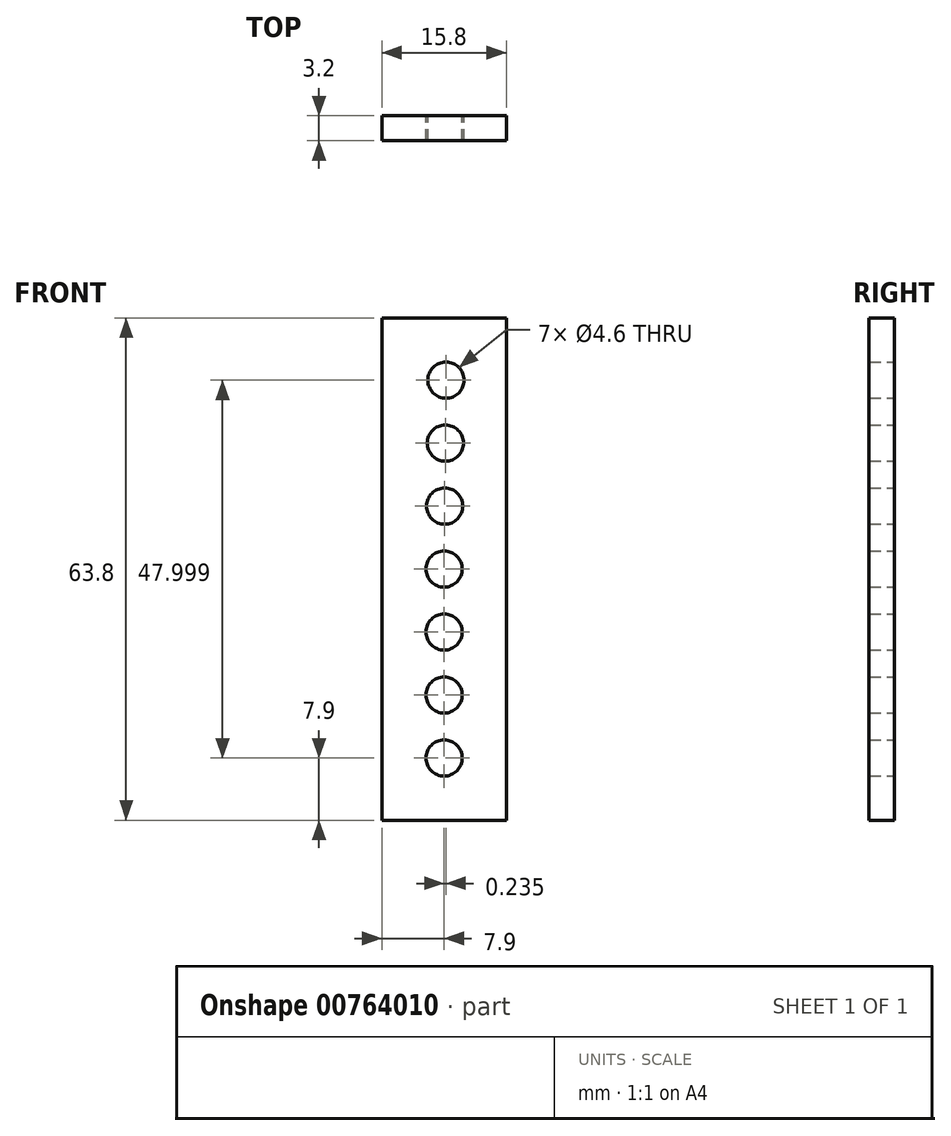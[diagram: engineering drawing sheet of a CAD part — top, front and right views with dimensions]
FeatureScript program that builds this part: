
annotation { "Feature Type Name" : "Feature", "Feature Type Description" : "" }
export const myFeature = defineFeature(function(context is Context, id is Id, definition is map)
    precondition{}
    {
        {
            var Q0;
            Q0=qCreatedBy(makeId("Front.planeOp"),FACE);
            var sketch = newSketch(context, id + "F0", { "sketchPlane" : qUnion([Q0])});
            skLineSegment(sketch, "E0.bottom", {"start": v(7.9, 31.9) * mm, "end": v(-7.9, 31.9) * mm});
            skLineSegment(sketch, "E0.top", {"start": v(7.9, -31.9) * mm, "end": v(-7.9, -31.9) * mm});
            skLineSegment(sketch, "E0.left", {"start": v(7.9, 31.9) * mm, "end": v(7.9, -31.9) * mm});
            skLineSegment(sketch, "E0.right", {"start": v(-7.9, 31.9) * mm, "end": v(-7.9, -31.9) * mm});
            skPoint(sketch, "E0.middle", {"position": v(0, 0) * mm});
            skCircle(sketch, "E1", {"center": v(0, 0) * mm, "radius": 2.3 * mm});
            skCircle(sketch, "E2.1.0.0", {"center": v(0, -8) * mm, "radius": 2.3 * mm});
            skCircle(sketch, "E2.2.0.0", {"center": v(0, -16) * mm, "radius": 2.3 * mm});
            skCircle(sketch, "E2.3.0.0", {"center": v(0, -24) * mm, "radius": 2.3 * mm});
            skLineSegment(sketch, "E2.direction1", {"start": v(0, 0) * mm, "end": v(0, -8) * mm, "construction": true});
            skCircle(sketch, "E3.1.0.0", {"center": v(0.08, 8) * mm, "radius": 2.3 * mm});
            skCircle(sketch, "E3.2.0.0", {"center": v(0.16, 16) * mm, "radius": 2.3 * mm});
            skCircle(sketch, "E3.3.0.0", {"center": v(0.24, 24) * mm, "radius": 2.3 * mm});
            skLineSegment(sketch, "E3.direction1", {"start": v(0, 0) * mm, "end": v(0.08, 8) * mm, "construction": true});
            skSolve(sketch);
        }
        {
            var Q0;
            Q0=makeQuery(id+"F0.imprint","IMPRINT",FACE,{"disambiguationData":[TD([[makeQuery(id+"F0.imprint","IMPRINT",EDGE,{"derivedFrom":sQuery(id+"F0.wireOp",EDGE,"E0.bottom")}),1.0]])]});
            extrude(context, id + "F1", {"entities" : qUnion([Q0]), "depth" : 3.2 * mm, "offsetDistance" : 25 * mm});
        }
    });
